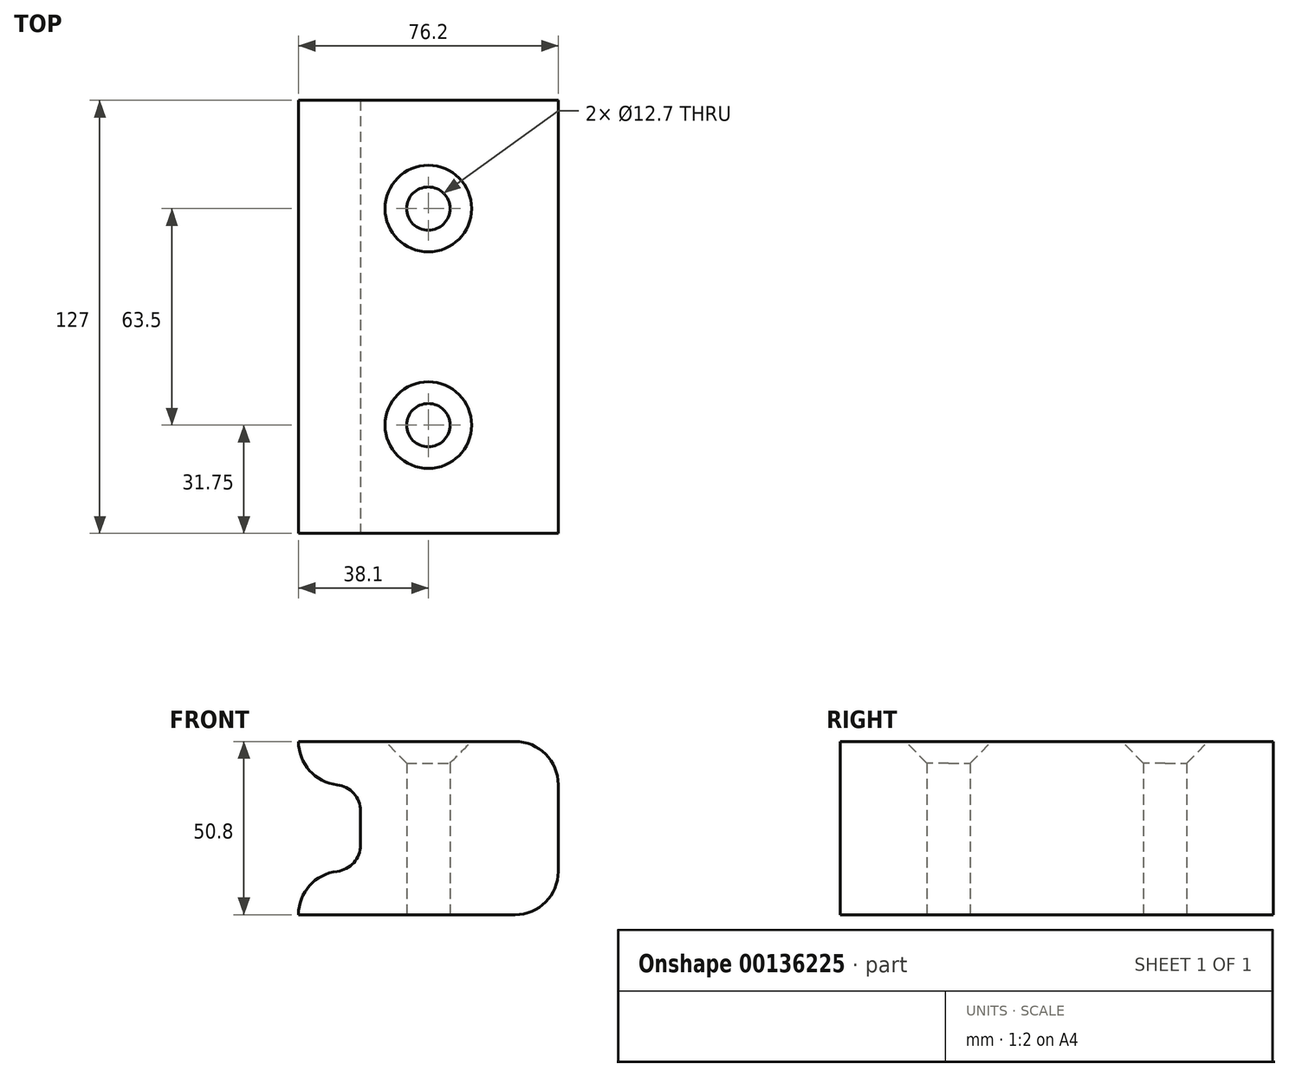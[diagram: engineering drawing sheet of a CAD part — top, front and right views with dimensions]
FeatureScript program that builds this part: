
annotation { "Feature Type Name" : "Feature", "Feature Type Description" : "" }
export const myFeature = defineFeature(function(context is Context, id is Id, definition is map)
    precondition{}
    {
        {
            var Q0;
            Q0=qCreatedBy(makeId("Front.planeOp"),FACE);
            var sketch = newSketch(context, id + "F0", { "sketchPlane" : qUnion([Q0])});
            skLineSegment(sketch, "E0.bottom", {"start": v(0, 0) * mm, "end": v(76.2, 0) * mm});
            skLineSegment(sketch, "E0.top", {"start": v(0, 50.8) * mm, "end": v(76.2, 50.8) * mm});
            skLineSegment(sketch, "E0.left", {"start": v(0, 0) * mm, "end": v(0, 50.8) * mm});
            skLineSegment(sketch, "E0.right", {"start": v(76.2, 0) * mm, "end": v(76.2, 50.8) * mm});
            skSolve(sketch);
        }
        {
            var Q0;
            Q0 = qSketchRegion(id + "F0", true);
            extrude(context, id + "F1", {"entities" : qUnion([Q0]), "depth" : 127 * mm});
        }
        {
            var Q0;
            Q0=makeQuery(id+"F1.opExtrude","CAP_FACE",FACE,{"disambiguationData":[OSD([sQuery(id+"F0.wireOp",EDGE,"E0.bottom"),sQuery(id+"F0.wireOp",EDGE,"E0.top"),sQuery(id+"F0.wireOp",EDGE,"E0.left"),sQuery(id+"F0.wireOp",EDGE,"E0.right")])],"isStart":false});
            var sketch = newSketch(context, id + "F2", { "sketchPlane" : qUnion([Q0])});
            skArc(sketch, "E1", {"start": v(0, 50.8) * mm, "mid": v(3.24, 42.3) * mm, "end": v(11.32, 38.1) * mm});
            skArc(sketch, "E2", {"start": v(11.32, 12.7) * mm, "mid": v(3.24, 8.5) * mm, "end": v(0, 0) * mm});
            skArc(sketch, "E3", {"start": v(18.18, 30.4) * mm, "mid": v(16.21, 35.56) * mm, "end": v(11.32, 38.1) * mm});
            skArc(sketch, "E4", {"start": v(11.32, 12.7) * mm, "mid": v(16.21, 15.24) * mm, "end": v(18.18, 20.4) * mm});
            skLineSegment(sketch, "E5", {"start": v(18.18, 30.4) * mm, "end": v(18.18, 20.4) * mm});
            skLineSegment(sketch, "E6", {"start": v(11.32, 38.1) * mm, "end": v(11.32, 12.7) * mm, "construction": true});
            skLineSegment(sketch, "E7", {"start": v(0, 25.4) * mm, "end": v(11.32, 25.4) * mm, "construction": true});
            skLineSegment(sketch, "E8", {"start": v(0, 50.8) * mm, "end": v(0, 0) * mm});
            skSolve(sketch);
        }
        {
            var Q0;
            Q0 = qSketchRegion(id + "F2", true);
            extrude(context, id + "F3", {"entities" : qUnion([Q0]), "operationType" : NewBodyOperationType.REMOVE, "endBound" : BoundingType.THROUGH_ALL, "oppositeDirection" : true, "depth" : 25.4 * mm});
        }
        {
            var Q0;
            Q0=makeQuery(id+"F1.opExtrude","SWEPT_EDGE",EDGE,{"disambiguationData":[OSD([sQuery(id+"F0.wireOp",EDGE,"E0.top"),sQuery(id+"F0.wireOp",EDGE,"E0.right")])]});
            var Q1;
            Q1=makeQuery(id+"F1.opExtrude","SWEPT_EDGE",EDGE,{"disambiguationData":[OSD([sQuery(id+"F0.wireOp",EDGE,"E0.bottom"),sQuery(id+"F0.wireOp",EDGE,"E0.right")])]});
            fillet(context, id + "F4", {"entities" : qUnion([Q0, Q1]), "radius" : 12.7 * mm, "tangentPropagation" : true, "allowEdgeOverflow" : false});
        }
        {
            var Q0;
            Q0=makeQuery(id+"F1.opExtrude","SWEPT_FACE",FACE,{"disambiguationData":[OSD([sQuery(id+"F0.wireOp",EDGE,"E0.bottom")])]});
            var sketch = newSketch(context, id + "F5", { "sketchPlane" : qUnion([Q0])});
            skCircle(sketch, "E9", {"center": v(38.1, 95.25) * mm, "radius": 6.35 * mm});
            skCircle(sketch, "E10", {"center": v(38.1, 31.75) * mm, "radius": 6.35 * mm});
            skLineSegment(sketch, "E11", {"start": v(38.1, 95.25) * mm, "end": v(38.1, 31.75) * mm});
            skLineSegment(sketch, "E12", {"start": v(0, 63.5) * mm, "end": v(38.1, 63.5) * mm});
            skSolve(sketch);
        }
        {
            var Q0;
            Q0 = qSketchRegion(id + "F5", true);
            extrude(context, id + "F6", {"entities" : qUnion([Q0]), "operationType" : NewBodyOperationType.REMOVE, "endBound" : BoundingType.THROUGH_ALL, "oppositeDirection" : true, "depth" : 25.4 * mm});
        }
        {
            var Q0;
            Q0=makeQuery(id+"F6.boolean.opBoolean","INTERSECT",EDGE,{"derivedFrom":[makeQuery(id+"F1.opExtrude","SWEPT_FACE",FACE,{"disambiguationData":[OSD([sQuery(id+"F0.wireOp",EDGE,"E0.top")])]}),makeQuery(id+"F6.opExtrude","SWEPT_FACE",FACE,{"disambiguationData":[OSD([sQuery(id+"F5.wireOp",EDGE,"E9")])]})]});
            var Q1;
            Q1=makeQuery(id+"F6.boolean.opBoolean","INTERSECT",EDGE,{"derivedFrom":[makeQuery(id+"F1.opExtrude","SWEPT_FACE",FACE,{"disambiguationData":[OSD([sQuery(id+"F0.wireOp",EDGE,"E0.top")])]}),makeQuery(id+"F6.opExtrude","SWEPT_FACE",FACE,{"disambiguationData":[OSD([sQuery(id+"F5.wireOp",EDGE,"E10")])]})]});
            chamfer(context, id + "F7", {"entities" : qUnion([Q0, Q1]), "width" : 6.35 * mm, "tangentPropagation" : true});
        }
    });
